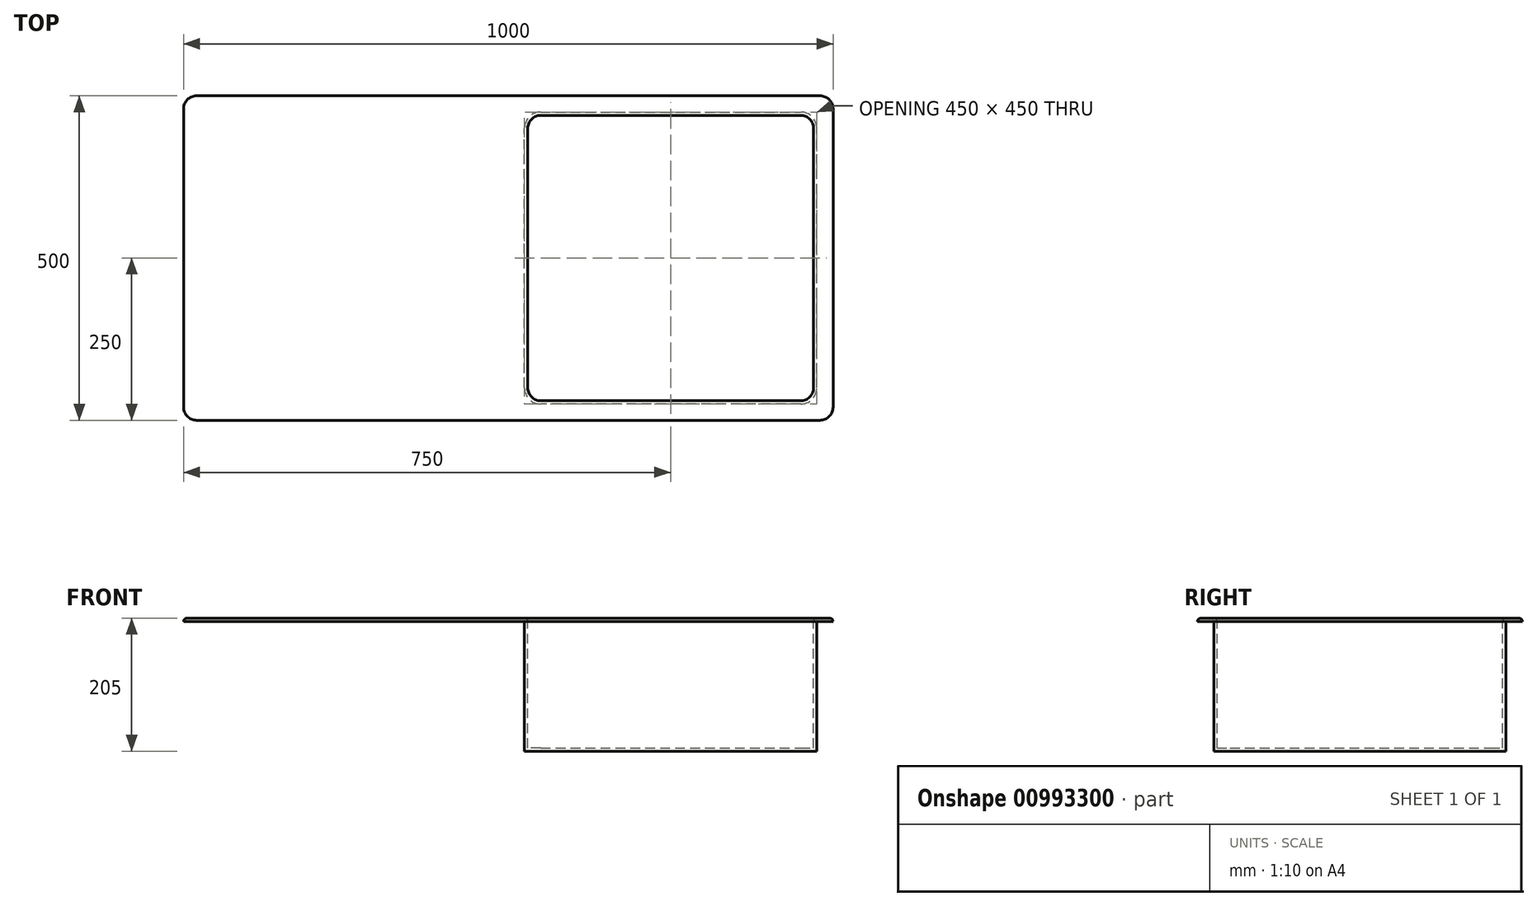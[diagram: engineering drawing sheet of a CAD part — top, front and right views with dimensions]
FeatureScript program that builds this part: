
annotation { "Feature Type Name" : "Feature", "Feature Type Description" : "" }
export const myFeature = defineFeature(function(context is Context, id is Id, definition is map)
    precondition{}
    {
        {
            var Q0;
            Q0=qCreatedBy(makeId("Top.planeOp"),FACE);
            var sketch = newSketch(context, id + "F0", { "sketchPlane" : qUnion([Q0])});
            skLineSegment(sketch, "E0.bottom", {"start": v(0, 0) * mm, "end": v(1000, 0) * mm});
            skLineSegment(sketch, "E0.top", {"start": v(0, 500) * mm, "end": v(1000, 500) * mm});
            skLineSegment(sketch, "E0.left", {"start": v(0, 0) * mm, "end": v(0, 500) * mm});
            skLineSegment(sketch, "E0.right", {"start": v(1000, 0) * mm, "end": v(1000, 500) * mm});
            skSolve(sketch);
        }
        {
            var Q0;
            Q0 = qSketchRegion(id + "F0", true);
            extrude(context, id + "F1", {"entities" : qUnion([Q0]), "oppositeDirection" : true, "depth" : 250 * mm, "offsetDistance" : 25 * mm});
        }
        {
            var Q0;
            Q0=qCreatedBy(makeId("Top.planeOp"),FACE);
            var sketch = newSketch(context, id + "F2", { "sketchPlane" : qUnion([Q0])});
            skLineSegment(sketch, "E1.bottom", {"start": v(530, 30) * mm, "end": v(970, 30) * mm});
            skLineSegment(sketch, "E1.top", {"start": v(530, 470) * mm, "end": v(970, 470) * mm});
            skLineSegment(sketch, "E1.left", {"start": v(530, 30) * mm, "end": v(530, 470) * mm});
            skLineSegment(sketch, "E1.right", {"start": v(970, 30) * mm, "end": v(970, 470) * mm});
            skSolve(sketch);
        }
        {
            var Q0;
            Q0 = qSketchRegion(id + "F2", true);
            extrude(context, id + "F3", {"entities" : qUnion([Q0]), "operationType" : NewBodyOperationType.REMOVE, "oppositeDirection" : true, "depth" : 200 * mm, "offsetDistance" : 25 * mm});
        }
        {
            var Q0;
            Q0=makeQuery(id+"F1.opExtrude","SWEPT_EDGE",EDGE,{"disambiguationData":[OSD([sQuery(id+"F0.wireOp",EDGE,"E0.bottom"),sQuery(id+"F0.wireOp",EDGE,"E0.left")])]});
            var Q1;
            Q1=makeQuery(id+"F1.opExtrude","SWEPT_EDGE",EDGE,{"disambiguationData":[OSD([sQuery(id+"F0.wireOp",EDGE,"E0.bottom"),sQuery(id+"F0.wireOp",EDGE,"E0.right")])]});
            var Q2;
            Q2=makeQuery(id+"F1.opExtrude","SWEPT_EDGE",EDGE,{"disambiguationData":[OSD([sQuery(id+"F0.wireOp",EDGE,"E0.top"),sQuery(id+"F0.wireOp",EDGE,"E0.left")])]});
            var Q3;
            Q3=makeQuery(id+"F3.boolean.opBoolean","COPY",EDGE,{"derivedFrom":makeQuery(id+"F3.opExtrude","SWEPT_EDGE",EDGE,{"disambiguationData":[OSD([sQuery(id+"F2.wireOp",EDGE,"E1.top"),sQuery(id+"F2.wireOp",EDGE,"E1.left")])]})});
            var Q4;
            Q4=makeQuery(id+"F3.boolean.opBoolean","COPY",EDGE,{"derivedFrom":makeQuery(id+"F3.opExtrude","SWEPT_EDGE",EDGE,{"disambiguationData":[OSD([sQuery(id+"F2.wireOp",EDGE,"E1.top"),sQuery(id+"F2.wireOp",EDGE,"E1.right")])]})});
            var Q5;
            Q5=makeQuery(id+"F3.boolean.opBoolean","COPY",EDGE,{"derivedFrom":makeQuery(id+"F3.opExtrude","SWEPT_EDGE",EDGE,{"disambiguationData":[OSD([sQuery(id+"F2.wireOp",EDGE,"E1.bottom"),sQuery(id+"F2.wireOp",EDGE,"E1.left")])]})});
            var Q6;
            Q6=makeQuery(id+"F3.boolean.opBoolean","COPY",EDGE,{"derivedFrom":makeQuery(id+"F3.opExtrude","SWEPT_EDGE",EDGE,{"disambiguationData":[OSD([sQuery(id+"F2.wireOp",EDGE,"E1.bottom"),sQuery(id+"F2.wireOp",EDGE,"E1.right")])]})});
            var Q7;
            Q7=makeQuery(id+"F3.boolean.opBoolean","COPY",EDGE,{"derivedFrom":makeQuery(id+"F3.opExtrude","CAP_EDGE",EDGE,{"disambiguationData":[OSD([sQuery(id+"F2.wireOp",EDGE,"E1.left")])],"isStart":true})});
            var Q8;
            Q8=makeQuery(id+"F1.opExtrude","SWEPT_EDGE",EDGE,{"disambiguationData":[OSD([sQuery(id+"F0.wireOp",EDGE,"E0.top"),sQuery(id+"F0.wireOp",EDGE,"E0.right")])]});
            fillet(context, id + "F4", {"entities" : qUnion([Q0, Q1, Q2, Q3, Q4, Q5, Q6, Q7, Q8]), "radius" : 20 * mm, "tangentPropagation" : true, "allowEdgeOverflow" : false});
        }
        {
            var Q0;
            Q0=makeQuery(id+"F1.opExtrude","CAP_FACE",FACE,{"disambiguationData":[OSD([sQuery(id+"F0.wireOp",EDGE,"E0.bottom"),sQuery(id+"F0.wireOp",EDGE,"E0.top"),sQuery(id+"F0.wireOp",EDGE,"E0.left"),sQuery(id+"F0.wireOp",EDGE,"E0.right")])],"isStart":true});
            fillet(context, id + "F5", {"entities" : qUnion([Q0]), "radius" : 5 * mm, "tangentPropagation" : true, "allowEdgeOverflow" : false});
        }
        {
            var Q0;
            Q0=makeQuery(id+"F1.opExtrude","CAP_FACE",FACE,{"disambiguationData":[OSD([sQuery(id+"F0.wireOp",EDGE,"E0.bottom"),sQuery(id+"F0.wireOp",EDGE,"E0.top"),sQuery(id+"F0.wireOp",EDGE,"E0.left"),sQuery(id+"F0.wireOp",EDGE,"E0.right")])],"isStart":false});
            var Q1;
            Q1=makeQuery(id+"F1.opExtrude","SWEPT_FACE",FACE,{"disambiguationData":[OSD([sQuery(id+"F0.wireOp",EDGE,"E0.bottom")])]});
            var Q2;
            Q2=makeQuery(id+"F1.opExtrude","SWEPT_FACE",FACE,{"disambiguationData":[OSD([sQuery(id+"F0.wireOp",EDGE,"E0.right")])]});
            var Q3;
            Q3=makeQuery(id+"F4.opFillet","BLEND_FACE",FACE,{"disambiguationData":[OSD([sQuery(id+"F0.wireOp",EDGE,"E0.bottom"),sQuery(id+"F0.wireOp",EDGE,"E0.right")])]});
            var Q4;
            Q4=makeQuery(id+"F1.opExtrude","SWEPT_FACE",FACE,{"disambiguationData":[OSD([sQuery(id+"F0.wireOp",EDGE,"E0.left")])]});
            var Q5;
            Q5=makeQuery(id+"F4.opFillet","BLEND_FACE",FACE,{"disambiguationData":[OSD([sQuery(id+"F0.wireOp",EDGE,"E0.bottom"),sQuery(id+"F0.wireOp",EDGE,"E0.left")])]});
            var Q6;
            Q6=makeQuery(id+"F4.opFillet","BLEND_FACE",FACE,{"disambiguationData":[OSD([sQuery(id+"F0.wireOp",EDGE,"E0.top"),sQuery(id+"F0.wireOp",EDGE,"E0.left")])]});
            var Q7;
            Q7=makeQuery(id+"F1.opExtrude","SWEPT_FACE",FACE,{"disambiguationData":[OSD([sQuery(id+"F0.wireOp",EDGE,"E0.top")])]});
            var Q8;
            Q8=makeQuery(id+"F4.opFillet","BLEND_FACE",FACE,{"disambiguationData":[OSD([sQuery(id+"F0.wireOp",EDGE,"E0.top"),sQuery(id+"F0.wireOp",EDGE,"E0.right")])]});
            shell(context, id + "F6", {"entities" : qUnion([Q0, Q1, Q2, Q3, Q4, Q5, Q6, Q7, Q8]), "thickness" : 5 * mm});
        }
    });
